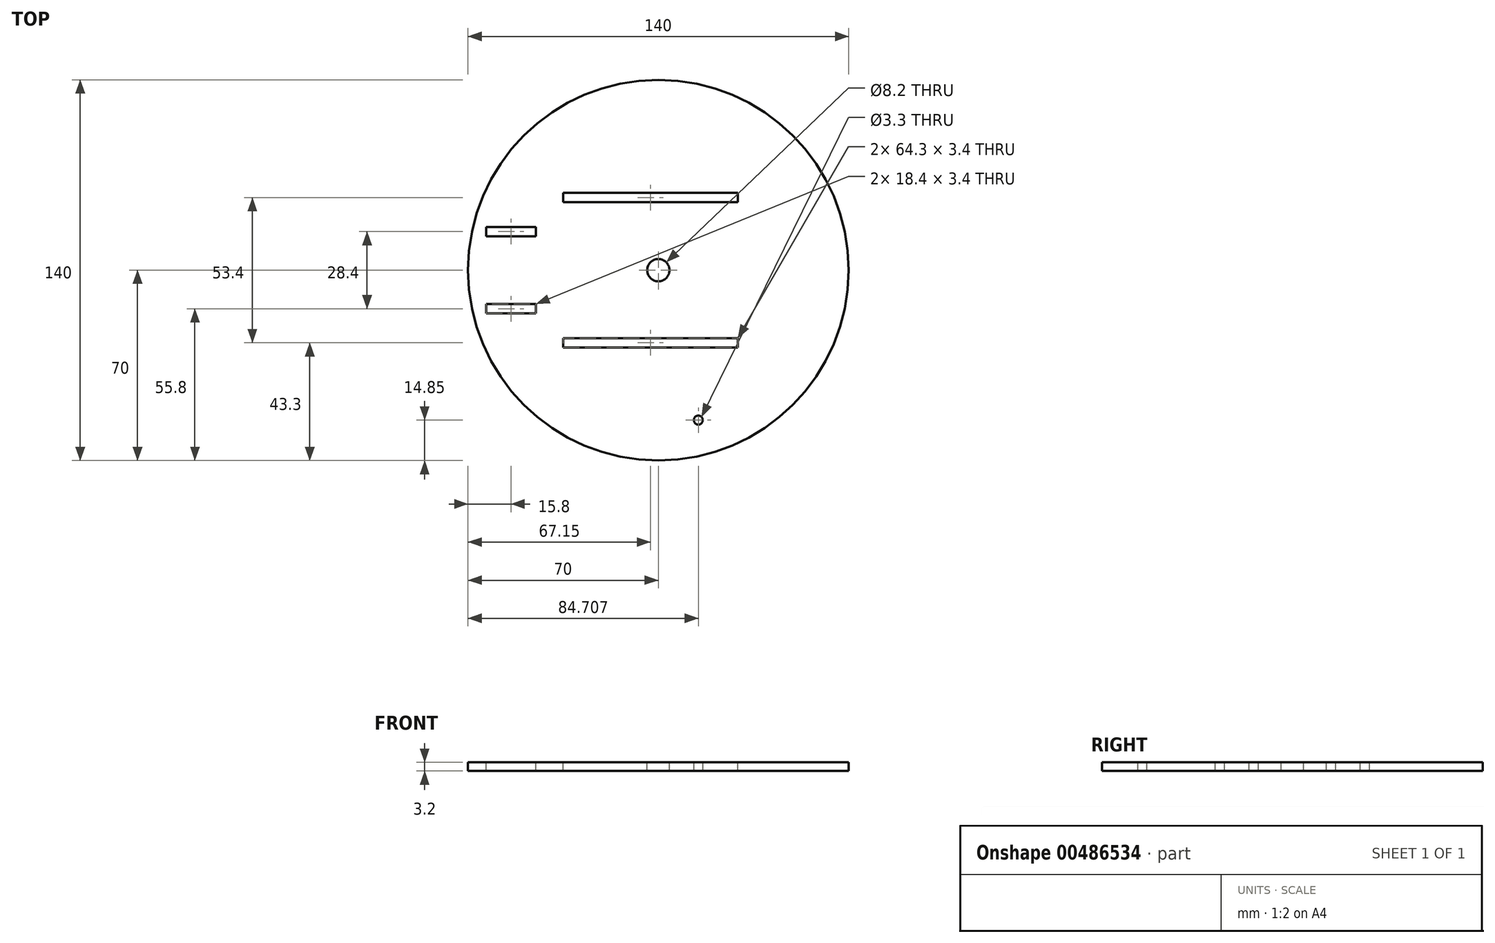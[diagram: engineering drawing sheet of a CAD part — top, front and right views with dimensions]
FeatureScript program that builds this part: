
annotation { "Feature Type Name" : "Feature", "Feature Type Description" : "" }
export const myFeature = defineFeature(function(context is Context, id is Id, definition is map)
    precondition{}
    {
        {
            var Q0;
            Q0=qCreatedBy(makeId("Top.planeOp"),FACE);
            var sketch = newSketch(context, id + "F0", { "sketchPlane" : qUnion([Q0])});
            skCircle(sketch, "E0", {"center": v(0, 0) * mm, "radius": 70 * mm});
            skLineSegment(sketch, "E1.bottom", {"start": v(-35, 28.4) * mm, "end": v(29.3, 28.4) * mm});
            skLineSegment(sketch, "E1.top", {"start": v(-35, 25) * mm, "end": v(29.3, 25) * mm});
            skLineSegment(sketch, "E1.left", {"start": v(-35, 28.4) * mm, "end": v(-35, 25) * mm});
            skLineSegment(sketch, "E1.right", {"start": v(29.3, 28.4) * mm, "end": v(29.3, 25) * mm});
            skLineSegment(sketch, "E2", {"start": v(-35, -25) * mm, "end": v(34.9, -25) * mm});
            skLineSegment(sketch, "E3.bottom", {"start": v(-35, -25) * mm, "end": v(29.3, -25) * mm});
            skLineSegment(sketch, "E3.top", {"start": v(-35, -28.4) * mm, "end": v(29.3, -28.4) * mm});
            skLineSegment(sketch, "E3.left", {"start": v(-35, -25) * mm, "end": v(-35, -28.4) * mm});
            skLineSegment(sketch, "E3.right", {"start": v(29.3, -25) * mm, "end": v(29.3, -28.4) * mm});
            skLineSegment(sketch, "E4.bottom", {"start": v(-63.4, 12.5) * mm, "end": v(-45, 12.5) * mm});
            skLineSegment(sketch, "E4.top", {"start": v(-63.4, 15.9) * mm, "end": v(-45, 15.9) * mm});
            skLineSegment(sketch, "E4.left", {"start": v(-63.4, 12.5) * mm, "end": v(-63.4, 15.9) * mm});
            skLineSegment(sketch, "E4.right", {"start": v(-45, 12.5) * mm, "end": v(-45, 15.9) * mm});
            skLineSegment(sketch, "E5.bottom", {"start": v(-63.4, -15.9) * mm, "end": v(-45, -15.9) * mm});
            skLineSegment(sketch, "E5.top", {"start": v(-63.4, -12.5) * mm, "end": v(-45, -12.5) * mm});
            skLineSegment(sketch, "E5.left", {"start": v(-63.4, -15.9) * mm, "end": v(-63.4, -12.5) * mm});
            skLineSegment(sketch, "E5.right", {"start": v(-45, -15.9) * mm, "end": v(-45, -12.5) * mm});
            skCircle(sketch, "E6", {"center": v(0, 0) * mm, "radius": 4.1 * mm});
            skSolve(sketch);
        }
        {
            var Q0;
            Q0=makeQuery(id+"F0.imprint","IMPRINT",FACE,{"disambiguationData":[TD([[makeQuery(id+"F0.imprint","IMPRINT",EDGE,{"derivedFrom":sQuery(id+"F0.wireOp",EDGE,"E0")}),1.0]])]});
            extrude(context, id + "F1", {"entities" : qUnion([Q0]), "oppositeDirection" : true, "depth" : 3.2 * mm, "offsetDistance" : 25 * mm});
        }
        {
            var Q0;
            Q0=qCreatedBy(makeId("Top.planeOp"),FACE);
            var sketch = newSketch(context, id + "F2", { "sketchPlane" : qUnion([Q0])});
            skCircle(sketch, "E7", {"center": v(14.7, -55.15) * mm, "radius": 1.65 * mm});
            skSolve(sketch);
        }
        {
            var Q0;
            Q0 = qSketchRegion(id + "F2", true);
            extrude(context, id + "F3", {"entities" : qUnion([Q0]), "operationType" : NewBodyOperationType.REMOVE, "oppositeDirection" : true, "depth" : 3.2 * mm, "offsetDistance" : 25 * mm});
        }
    });
